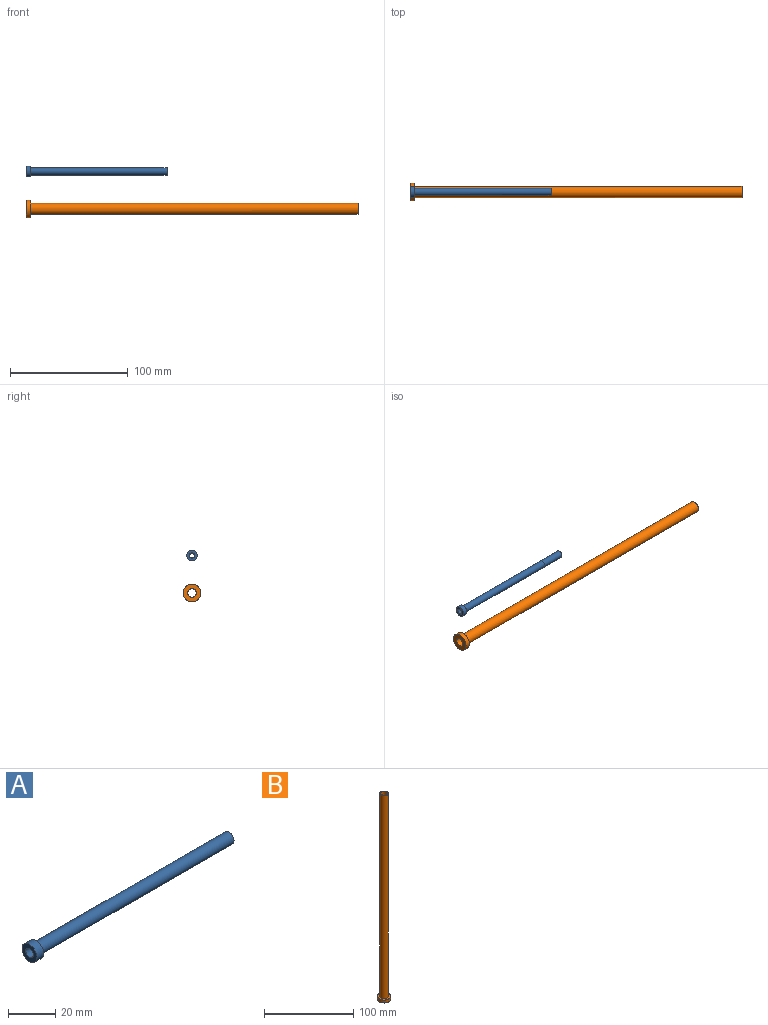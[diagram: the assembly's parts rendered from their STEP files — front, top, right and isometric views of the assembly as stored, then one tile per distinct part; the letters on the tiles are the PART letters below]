
ASSEMBLY  parts=2 mates=1
PART A: 9 faces, bbox 120x9x9 mm
  f0: cylinder r=2.05mm len=20mm, axis (1,0,0), area 257.6mm2, adj f1,f6
  f1: cone r=2.3mm half-angle=26.6deg, axis (-1,0,0), area 7.6mm2, adj f0,f2
  f2: cylinder r=2.3mm len=99.5mm, axis (1,0,0), area 1437.9mm2, adj f1,f8
  f3: torus R=3.2mm, axis (-1,0,0), area 6.1mm2, adj f4,f5
  f4: cylinder r=3mm len=115.8mm, axis (1,0,0), area 2182.8mm2, adj f3,f6
  f5: plane 9x9mm, normal (1,0,0), area 31.4mm2, adj f3,f7
  f6: plane 6x6mm, normal (1,0,0), area 15.1mm2, adj f0,f4
  f7: cylinder r=4.5mm len=9mm, axis (1,0,0), area 113.1mm2, adj f5,f8
  f8: plane 9x9mm, normal (-1,0,0), area 47mm2, adj f2,f7
PART B: 6 faces, bbox 15x15.3x282.6 mm
  f0: cylinder r=7.5mm len=15mm, axis (0,0,1), area 188.5mm2, adj f1,f2
  f1: plane 15.28x15mm, normal (0,0,1), area 107.3mm2, adj f0,f3
  f2: plane 15.28x15mm, normal (0,0,-1), area 134.9mm2, adj f0,f4
  f3: cylinder r=4.7mm len=278.55mm, axis (0,0,-1), area 8225.9mm2, adj f1,f5
  f4: cylinder r=3.65mm len=282.55mm, axis (0,0,-1), area 6479.9mm2, adj f2,f5
  f5: plane 9.53x9.42mm, normal (0,0,1), area 27.5mm2, adj f3,f4
PLACE A t=(0,0,31.9)mm
PLACE B rot(axis=(0,1,0),90deg) t=(260,-73.29,85.94)mm
MATE planar B.f0 <-> A.f0  axis (-1,0,0) through (0,0,0)mm
